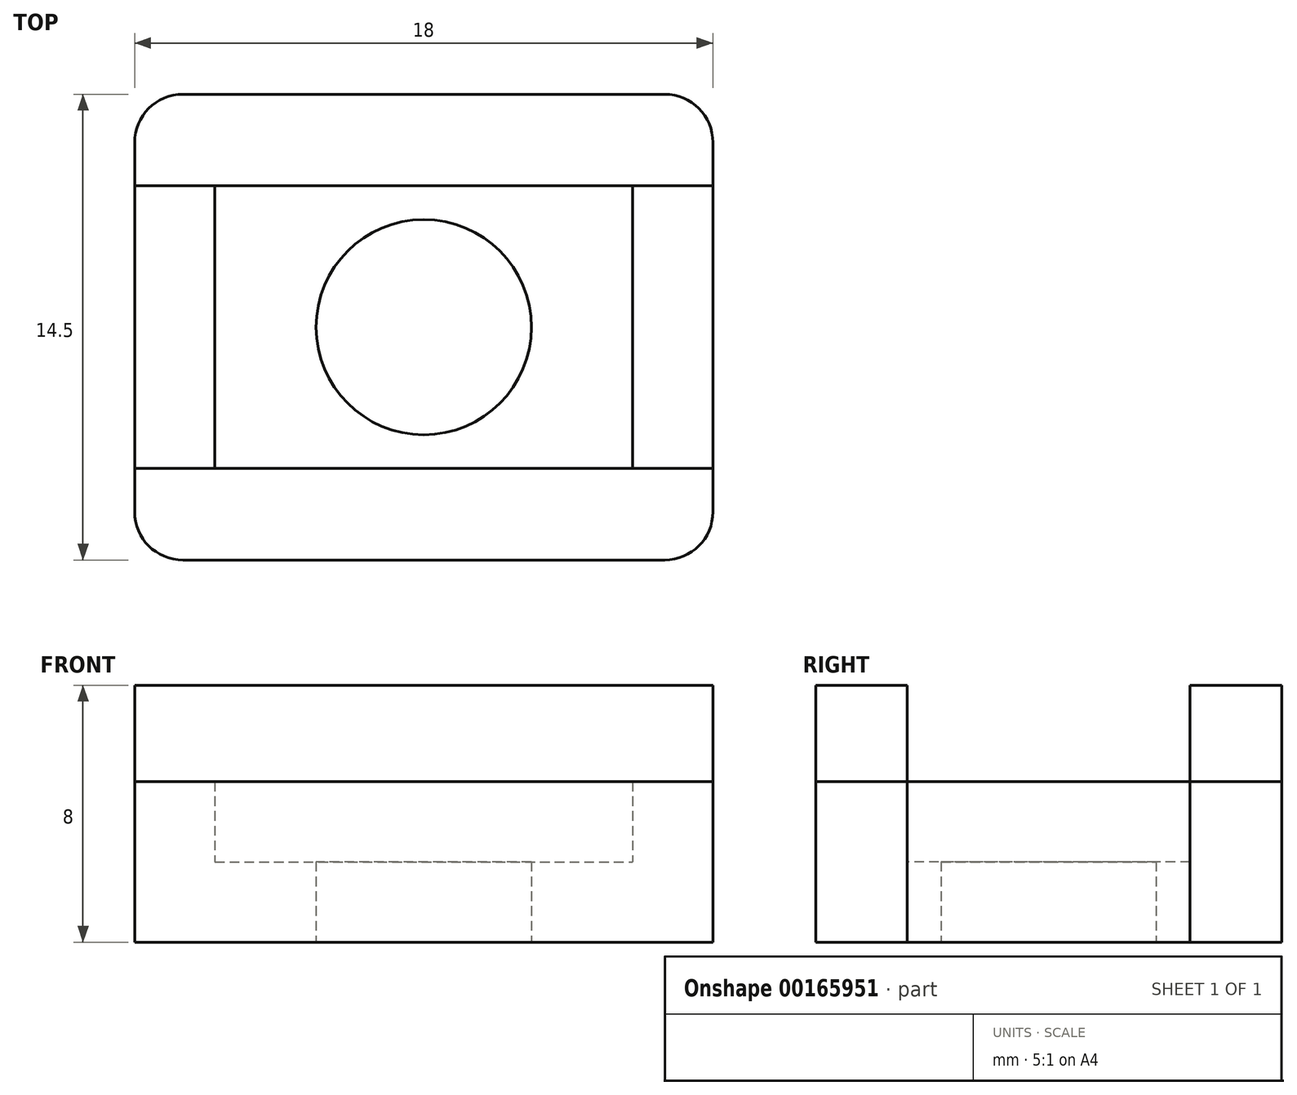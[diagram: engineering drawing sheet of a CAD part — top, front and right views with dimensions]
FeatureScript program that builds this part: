
annotation { "Feature Type Name" : "Feature", "Feature Type Description" : "" }
export const myFeature = defineFeature(function(context is Context, id is Id, definition is map)
    precondition{}
    {
        {
            var Q0;
            Q0=qCreatedBy(makeId("Top.planeOp"),FACE);
            var sketch = newSketch(context, id + "F0", { "sketchPlane" : qUnion([Q0])});
            skLineSegment(sketch, "E0.bottom", {"start": v(-7.5, 7.25) * mm, "end": v(7.5, 7.25) * mm});
            skLineSegment(sketch, "E0.top", {"start": v(-7.5, -7.25) * mm, "end": v(7.5, -7.25) * mm});
            skLineSegment(sketch, "E0.left", {"start": v(-9, 5.75) * mm, "end": v(-9, -5.75) * mm});
            skLineSegment(sketch, "E0.right", {"start": v(9, 5.75) * mm, "end": v(9, -5.75) * mm});
            skLineSegment(sketch, "E1.bottom", {"start": v(-6.5, 4.4) * mm, "end": v(6.5, 4.4) * mm});
            skLineSegment(sketch, "E1.top", {"start": v(-6.5, -4.4) * mm, "end": v(6.5, -4.4) * mm});
            skLineSegment(sketch, "E1.left", {"start": v(-6.5, 4.4) * mm, "end": v(-6.5, -4.4) * mm});
            skLineSegment(sketch, "E1.right", {"start": v(6.5, 4.4) * mm, "end": v(6.5, -4.4) * mm});
            skCircle(sketch, "E2", {"center": v(0, 0) * mm, "radius": 3.35 * mm});
            skPoint(sketch, "E3.visualSharp", {"position": v(-9, 7.25) * mm});
            skArc(sketch, "E3.filletArc", {"start": v(-7.5, 7.25) * mm, "mid": v(-8.56, 6.81) * mm, "end": v(-9, 5.75) * mm});
            skPoint(sketch, "E4.visualSharp", {"position": v(9, 7.25) * mm});
            skArc(sketch, "E4.filletArc", {"start": v(9, 5.75) * mm, "mid": v(8.56, 6.81) * mm, "end": v(7.5, 7.25) * mm});
            skPoint(sketch, "E5.visualSharp", {"position": v(9, -7.25) * mm});
            skArc(sketch, "E5.filletArc", {"start": v(7.5, -7.25) * mm, "mid": v(8.56, -6.81) * mm, "end": v(9, -5.75) * mm});
            skPoint(sketch, "E6.visualSharp", {"position": v(-9, -7.25) * mm});
            skArc(sketch, "E6.filletArc", {"start": v(-9, -5.75) * mm, "mid": v(-8.56, -6.81) * mm, "end": v(-7.5, -7.25) * mm});
            skLineSegment(sketch, "E7.bottom", {"start": v(-9, 4.4) * mm, "end": v(9, 4.4) * mm});
            skLineSegment(sketch, "E7.top", {"start": v(-9, -4.4) * mm, "end": v(9, -4.4) * mm});
            skLineSegment(sketch, "E7.left", {"start": v(-9, 4.4) * mm, "end": v(-9, -4.4) * mm});
            skLineSegment(sketch, "E7.right", {"start": v(9, 4.4) * mm, "end": v(9, -4.4) * mm});
            skSolve(sketch);
        }
        {
            var Q0;
            Q0=makeQuery(id+"F0.imprint","IMPRINT",FACE,{"disambiguationData":[TD([[makeQuery(id+"F0.imprint","IMPRINT",EDGE,{"derivedFrom":sQuery(id+"F0.wireOp",EDGE,"E1.bottom")}),-1.0]])]});
            var Q1;
            {var subQ1=sQuery(id+"F0.wireOp",EDGE,"E1.left");Q1=makeQuery(id+"F0.imprint","IMPRINT",FACE,{"disambiguationData":[TD([[makeQuery(id+"F0.imprint","IMPRINT",EDGE,{"derivedFrom":subQ1}),1.0]])]});}
            extrude(context, id + "F1", {"entities" : qUnion([Q0, Q1]), "depth" : 2.5 * mm});
        }
        {
            var Q0;
            Q0 = qSketchRegion(id + "F0", true);
            extrude(context, id + "F2", {"entities" : qUnion([Q0]), "operationType" : NewBodyOperationType.ADD, "depth" : 5 * mm});
        }
        {
            var Q0;
            Q0=makeQuery(id+"F0.imprint","IMPRINT",FACE,{"disambiguationData":[TD([[makeQuery(id+"F0.imprint","IMPRINT",EDGE,{"derivedFrom":sQuery(id+"F0.wireOp",EDGE,"E0.bottom")}),-1.0]])]});
            var Q1;
            Q1=makeQuery(id+"F0.imprint","IMPRINT",FACE,{"disambiguationData":[TD([[makeQuery(id+"F0.imprint","IMPRINT",EDGE,{"derivedFrom":sQuery(id+"F0.wireOp",EDGE,"E0.top")}),1.0]])]});
            extrude(context, id + "F3", {"entities" : qUnion([Q0, Q1]), "depth" : 8 * mm});
        }
    });
